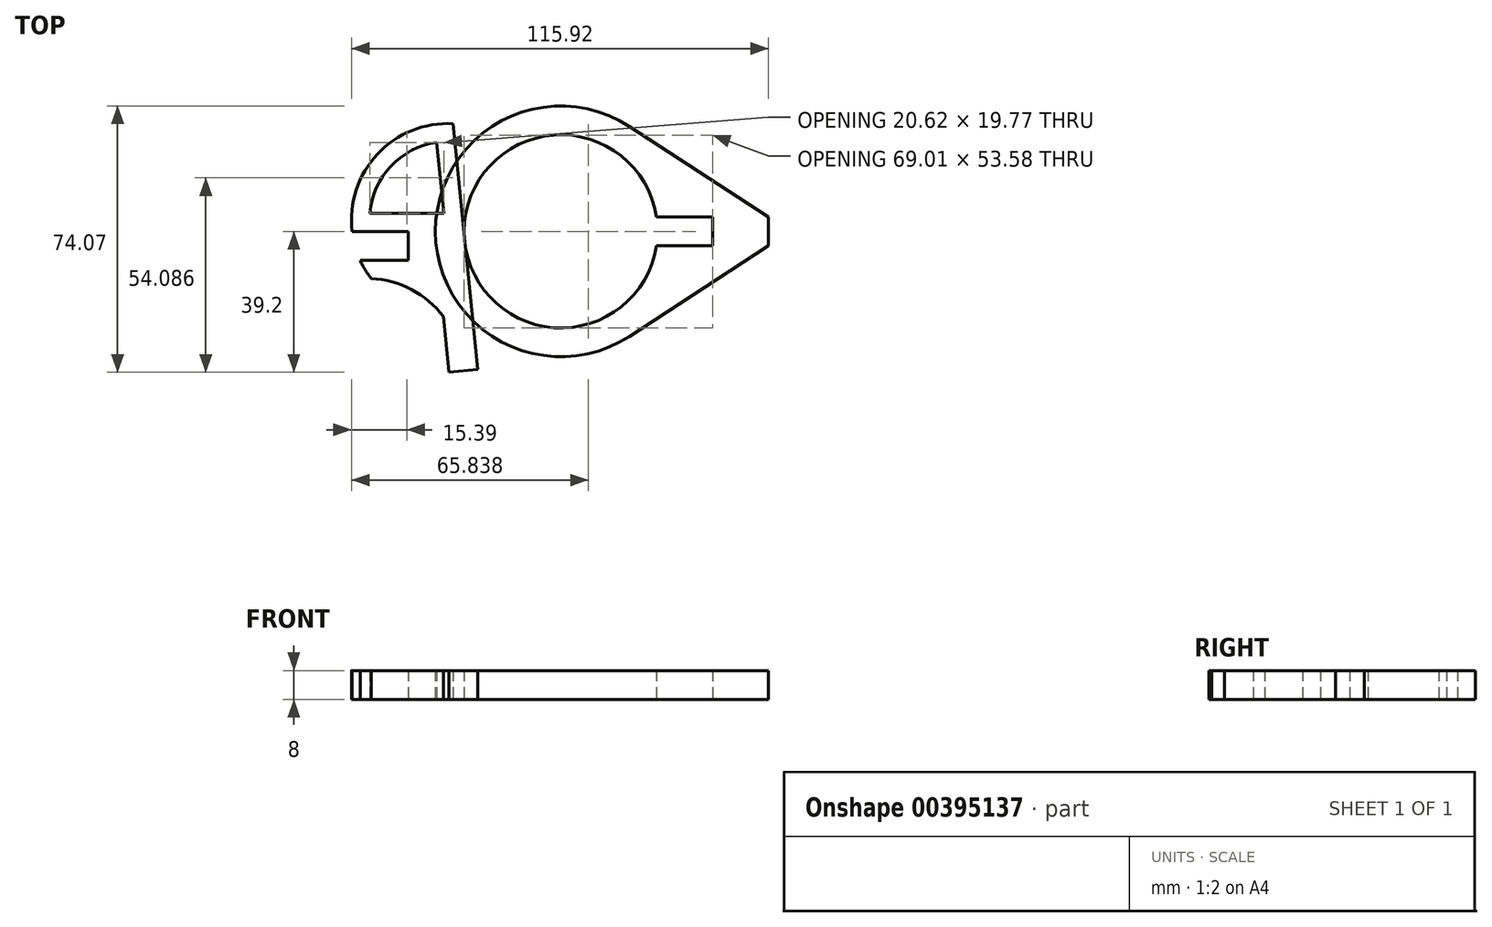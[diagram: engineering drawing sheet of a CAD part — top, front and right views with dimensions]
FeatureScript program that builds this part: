
annotation { "Feature Type Name" : "Feature", "Feature Type Description" : "" }
export const myFeature = defineFeature(function(context is Context, id is Id, definition is map)
    precondition{}
    {
        {
            assignVariable(context, id + "F0", {"name" : "gods", "anyValue" : 8});
        }
        {
            var Q0;
            Q0=qCreatedBy(makeId("Top.planeOp"),FACE);
            var sketch = newSketch(context, id + "F1", { "sketchPlane" : qUnion([Q0])});
            skLineSegment(sketch, "E0", {"start": v(57.72, 0) * mm, "end": v(57.72, 4) * mm});
            skLineSegment(sketch, "E1", {"start": v(57.72, 0) * mm, "end": v(57.72, -4) * mm});
            skCircle(sketch, "E2", {"center": v(0, 0) * mm, "radius": 26.87 * mm});
            skCircle(sketch, "E3.0", {"center": v(0, 0) * mm, "radius": 34.87 * mm});
            skLineSegment(sketch, "E4", {"start": v(57.72, 4) * mm, "end": v(14.15, 32.4) * mm});
            skLineSegment(sketch, "E5", {"start": v(57.72, -4) * mm, "end": v(13.28, -32.96) * mm});
            skLineSegment(sketch, "E6", {"start": v(0, 0) * mm, "end": v(0, 30) * mm, "construction": true});
            skLineSegment(sketch, "E7", {"start": v(0, 0) * mm, "end": v(0, -70) * mm, "construction": true});
            skLineSegment(sketch, "E8", {"start": v(0, -70) * mm, "end": v(-20, -70) * mm, "construction": true});
            skLineSegment(sketch, "E9", {"start": v(0, 30) * mm, "end": v(-30, 30) * mm, "construction": true});
            skLineSegment(sketch, "E10", {"start": v(-30, 30) * mm, "end": v(-20, -70) * mm, "construction": true});
            skLineSegment(sketch, "E11", {"start": v(-30, 30) * mm, "end": v(-33.98, 29.6) * mm, "construction": true});
            skLineSegment(sketch, "E12", {"start": v(-33.98, 29.6) * mm, "end": v(-27, -40.2) * mm, "construction": true});
            skCircle(sketch, "E13", {"center": v(-31.33, 3.13) * mm, "radius": 26.87 * mm, "construction": true});
            skLineSegment(sketch, "E14", {"start": v(-30, 30) * mm, "end": v(-68.05, 30) * mm, "construction": true});
            skLineSegment(sketch, "E15", {"start": v(-26.87, 0) * mm, "end": v(-42.44, 0) * mm, "construction": true});
            skLineSegment(sketch, "E16", {"start": v(-42.44, 0) * mm, "end": v(-58.02, 0) * mm, "construction": true});
            skLineSegment(sketch, "E17", {"start": v(42.14, 4) * mm, "end": v(26.57, 4) * mm});
            skLineSegment(sketch, "E18", {"start": v(42.14, -4) * mm, "end": v(26.57, -4) * mm});
            skLineSegment(sketch, "E19", {"start": v(42.14, 4) * mm, "end": v(57.72, 4) * mm, "construction": true});
            skLineSegment(sketch, "E20", {"start": v(42.14, -4) * mm, "end": v(57.72, -4) * mm, "construction": true});
            skLineSegment(sketch, "E21", {"start": v(42.14, -4) * mm, "end": v(42.14, 4) * mm});
            skSolve(sketch);
        }
        {
            var Q0;
            Q0=qCreatedBy(makeId("Top.planeOp"),FACE);
            var sketch = newSketch(context, id + "F2", { "sketchPlane" : qUnion([Q0])});
            skLineSegment(sketch, "E22.0", {"start": v(-30, 30) * mm, "end": v(-20, -70) * mm, "construction": true});
            skLineSegment(sketch, "E22.1", {"start": v(0, 30) * mm, "end": v(-30, 30) * mm, "construction": true});
            skLineSegment(sketch, "E22.2", {"start": v(0, -70) * mm, "end": v(-20, -70) * mm, "construction": true});
            skPoint(sketch, "E22.3", {"position": v(-20, -70) * mm});
            skPoint(sketch, "E22.4", {"position": v(-30, 30) * mm});
            skCircle(sketch, "E23.0", {"center": v(0, 0) * mm, "radius": 26.87 * mm, "construction": true});
            skCircle(sketch, "E24", {"center": v(-31.33, 3.13) * mm, "radius": 26.87 * mm, "construction": true});
            skLineSegment(sketch, "E25", {"start": v(-30, 30) * mm, "end": v(-32.36, 53.6) * mm, "construction": true});
            skLineSegment(sketch, "E26", {"start": v(-36.34, 53.2) * mm, "end": v(-30.45, -5.75) * mm, "construction": true});
            skLineSegment(sketch, "E27", {"start": v(-54.65, 16.48) * mm, "end": v(-8.02, -10.21) * mm, "construction": true});
            skLineSegment(sketch, "E28", {"start": v(-32.36, 53.6) * mm, "end": v(-36.34, 53.2) * mm});
            skLineSegment(sketch, "E29", {"start": v(-30, 30) * mm, "end": v(-62.05, 30) * mm, "construction": true});
            skLineSegment(sketch, "E30", {"start": v(-26.87, 0) * mm, "end": v(-42.44, 0) * mm, "construction": true});
            skLineSegment(sketch, "E31", {"start": v(-42.44, 0) * mm, "end": v(-58.02, 0) * mm});
            skLineSegment(sketch, "E32", {"start": v(-42.44, 0) * mm, "end": v(-42.44, -8.1) * mm});
            skLineSegment(sketch, "E33", {"start": v(-42.44, -8.1) * mm, "end": v(-55.74, -8.1) * mm});
            skLineSegment(sketch, "E34", {"start": v(-24.7, -22.9) * mm, "end": v(-47.31, -25.16) * mm, "construction": true});
            skLineSegment(sketch, "E35", {"start": v(-47.31, -25.16) * mm, "end": v(-45.76, -40.66) * mm, "construction": true});
            skLineSegment(sketch, "E36", {"start": v(-24.7, -22.9) * mm, "end": v(-30, 29.97) * mm});
            skLineSegment(sketch, "E37", {"start": v(-23.16, -38.4) * mm, "end": v(-31.12, -39.2) * mm});
            skLineSegment(sketch, "E38", {"start": v(-31.12, -39.2) * mm, "end": v(-32.67, -23.7) * mm});
            skLineSegment(sketch, "E39", {"start": v(-45.76, -40.66) * mm, "end": v(-31.12, -39.2) * mm});
            skLineSegment(sketch, "E40", {"start": v(-23.16, -38.4) * mm, "end": v(-24.7, -22.9) * mm});
            skArc(sketch, "E41", {"start": v(-58.02, 0) * mm, "mid": v(-50.96, 21.48) * mm, "end": v(-30, 29.97) * mm});
            skArc(sketch, "E42.0", {"start": v(-53.12, 5) * mm, "mid": v(-47.24, 18.13) * mm, "end": v(-34.48, 24.77) * mm});
            skLineSegment(sketch, "E43", {"start": v(-46, 0) * mm, "end": v(-46, 5) * mm, "construction": true});
            skLineSegment(sketch, "E44", {"start": v(-46, 5) * mm, "end": v(-53.12, 5) * mm});
            skLineSegment(sketch, "E45", {"start": v(-27.5, 5) * mm, "end": v(-32.5, 5) * mm});
            skLineSegment(sketch, "E46", {"start": v(-32.5, 5) * mm, "end": v(-34.48, 24.77) * mm});
            skLineSegment(sketch, "E47", {"start": v(-46, 5) * mm, "end": v(-32.5, 5) * mm});
            skLineSegment(sketch, "E48", {"start": v(-32.5, 5) * mm, "end": v(-32.5, 0) * mm, "construction": true});
            skLineSegment(sketch, "E49", {"start": v(-42.44, -8.1) * mm, "end": v(-42.44, -13.1) * mm, "construction": true});
            skLineSegment(sketch, "E50", {"start": v(-42.44, -13.1) * mm, "end": v(-52.74, -13.1) * mm, "construction": true});
            skLineSegment(sketch, "E51", {"start": v(-52.74, -13.1) * mm, "end": v(-32.67, -23.7) * mm, "construction": true});
            skArc(sketch, "E52", {"start": v(-52.74, -13.1) * mm, "mid": v(-43.88, -20.62) * mm, "end": v(-32.67, -23.7) * mm, "construction": true});
            skArc(sketch, "E53.MirrorCS", {"start": v(-52.74, -13.1) * mm, "mid": v(-41.53, -16.18) * mm, "end": v(-32.67, -23.7) * mm});
            skArc(sketch, "E54", {"start": v(-52.74, -13.1) * mm, "mid": v(-54.37, -10.68) * mm, "end": v(-55.74, -8.1) * mm});
            skSolve(sketch);
        }
        {
            var Q0;
            Q0=makeQuery(id+"F2.imprint","IMPRINT",FACE,{"disambiguationData":[TD([[makeQuery(id+"F2.imprint","IMPRINT",EDGE,{"derivedFrom":sQuery(id+"F2.wireOp",EDGE,"E31")}),-1.0]])]});
            extrude(context, id + "F3", {"entities" : qUnion([Q0]), "depth" : (getVariable(context, 'gods')) * mm});
        }
        {
            var Q0;
            {var subQ5=sQuery(id+"F1.wireOp",EDGE,"E17");var subQ7=sQuery(id+"F1.wireOp",EDGE,"E2");var subQ9=makeQuery(id+"F1.imprint","INTERSECT",VERTEX,{"derivedFrom":[subQ7,subQ5]});Q0=makeQuery(id+"F1.imprint","IMPRINT",FACE,{"disambiguationData":[TD([[makeQuery(id+"F1.imprint","IMPRINT",EDGE,{"disambiguationData":[TD([[subQ9,-1.0]])],"derivedFrom":subQ7}),-1.0]])]});}
            var Q1;
            {var subQ10=sQuery(id+"F1.wireOp",EDGE,"E0");Q1=makeQuery(id+"F1.imprint","IMPRINT",FACE,{"disambiguationData":[TD([[makeQuery(id+"F1.imprint","IMPRINT",EDGE,{"derivedFrom":subQ10}),1.0]])]});}
            extrude(context, id + "F4", {"entities" : qUnion([Q0, Q1]), "depth" : (getVariable(context, 'gods')) * mm});
        }
    });
